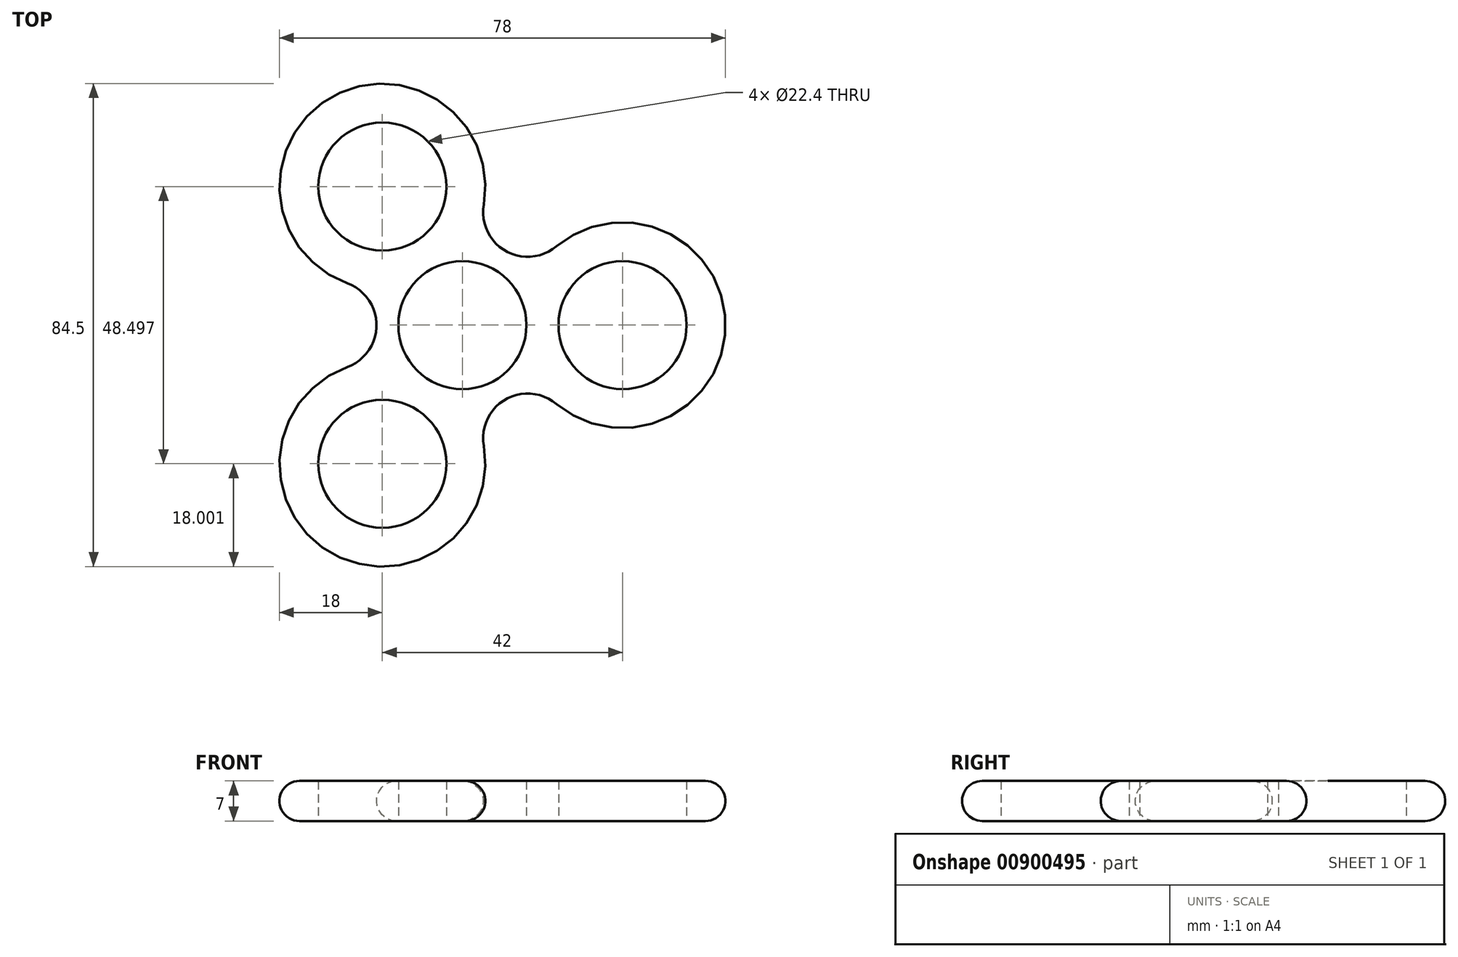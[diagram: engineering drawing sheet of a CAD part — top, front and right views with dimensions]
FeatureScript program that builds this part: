
annotation { "Feature Type Name" : "Feature", "Feature Type Description" : "" }
export const myFeature = defineFeature(function(context is Context, id is Id, definition is map)
    precondition{}
    {
        {
            assignVariable(context, id + "F0", {"name" : "w", "anyValue" : 7});
        }
        {
            var Q0;
            Q0=qCreatedBy(makeId("Top.planeOp"),FACE);
            var sketch = newSketch(context, id + "F1", { "sketchPlane" : qUnion([Q0])});
            skLineSegment(sketch, "E0", {"start": v(0, 0) * mm, "end": v(28, 0) * mm, "construction": true});
            skCircle(sketch, "E1", {"center": v(0, 0) * mm, "radius": 11.2 * mm});
            skCircle(sketch, "E2", {"center": v(28, 0) * mm, "radius": 11.2 * mm});
            skLineSegment(sketch, "E3", {"start": v(0, 0) * mm, "end": v(16.43, 13.79) * mm});
            skLineSegment(sketch, "E4", {"start": v(16.43, 13.79) * mm, "end": v(28, 0) * mm});
            skLineSegment(sketch, "E5", {"start": v(16.43, -13.79) * mm, "end": v(28, 0) * mm});
            skLineSegment(sketch, "E6", {"start": v(0, 0) * mm, "end": v(16.43, -13.79) * mm});
            skCircle(sketch, "E7", {"center": v(28, 0) * mm, "radius": 18 * mm});
            skCircle(sketch, "E8.cCircle", {"center": v(0, 0) * mm, "radius": 28 * mm, "construction": true});
            skLineSegment(sketch, "E8.0", {"start": v(28, 0) * mm, "end": v(14, -24.25) * mm, "construction": true});
            skLineSegment(sketch, "E8.1", {"start": v(14, -24.25) * mm, "end": v(-14, -24.25) * mm, "construction": true});
            skLineSegment(sketch, "E8.2", {"start": v(-14, -24.25) * mm, "end": v(-28, 0) * mm, "construction": true});
            skLineSegment(sketch, "E8.3", {"start": v(-28, 0) * mm, "end": v(-14, 24.25) * mm, "construction": true});
            skLineSegment(sketch, "E8.4", {"start": v(-14, 24.25) * mm, "end": v(14, 24.25) * mm, "construction": true});
            skLineSegment(sketch, "E8.5", {"start": v(14, 24.25) * mm, "end": v(28, 0) * mm, "construction": true});
            skCircle(sketch, "E9", {"center": v(-14, 24.25) * mm, "radius": 11.2 * mm});
            skCircle(sketch, "E10", {"center": v(-14, -24.25) * mm, "radius": 11.2 * mm});
            skLineSegment(sketch, "E11", {"start": v(0, 0) * mm, "end": v(-20.15, 7.33) * mm});
            skLineSegment(sketch, "E12", {"start": v(-20.15, 7.33) * mm, "end": v(-14, 24.25) * mm});
            skLineSegment(sketch, "E13", {"start": v(-14, 24.25) * mm, "end": v(3.73, 21.12) * mm});
            skLineSegment(sketch, "E14", {"start": v(3.73, 21.12) * mm, "end": v(0, 0) * mm});
            skLineSegment(sketch, "E15", {"start": v(0, 0) * mm, "end": v(-20.15, -7.33) * mm});
            skLineSegment(sketch, "E16", {"start": v(-20.15, -7.33) * mm, "end": v(-14, -24.25) * mm});
            skLineSegment(sketch, "E17", {"start": v(0, 0) * mm, "end": v(3.73, -21.12) * mm});
            skLineSegment(sketch, "E18", {"start": v(3.73, -21.12) * mm, "end": v(-14, -24.25) * mm});
            skCircle(sketch, "E19", {"center": v(-14, -24.25) * mm, "radius": 18 * mm});
            skCircle(sketch, "E20", {"center": v(-14, 24.25) * mm, "radius": 18 * mm});
            skLineSegment(sketch, "E21", {"start": v(3.73, 21.12) * mm, "end": v(8.02, 45.44) * mm, "construction": true});
            skArc(sketch, "E22", {"start": v(3.73, 21.12) * mm, "mid": v(7.5, 13) * mm, "end": v(16.43, 13.79) * mm});
            skLineSegment(sketch, "E23", {"start": v(-20.15, -7.33) * mm, "end": v(-52.36, -19.05) * mm, "construction": true});
            skArc(sketch, "E24", {"start": v(-20.15, -7.33) * mm, "mid": v(-15.02, 0) * mm, "end": v(-20.15, 7.33) * mm});
            skLineSegment(sketch, "E25", {"start": v(3.73, -21.12) * mm, "end": v(7.3, -41.37) * mm, "construction": true});
            skArc(sketch, "E26", {"start": v(3.73, -21.12) * mm, "mid": v(7.5, -13) * mm, "end": v(16.43, -13.79) * mm});
            skSolve(sketch);
        }
        {
            var Q0;
            {var subQ1=sQuery(id+"F1.wireOp",EDGE,"E4");var subQ4=sQuery(id+"F1.wireOp",EDGE,"E2");var subQ5=makeQuery(id+"F1.imprint","INTERSECT",VERTEX,{"derivedFrom":[subQ4,subQ1]});Q0=makeQuery(id+"F1.imprint","IMPRINT",FACE,{"disambiguationData":[TD([[makeQuery(id+"F1.imprint","IMPRINT",EDGE,{"disambiguationData":[TD([[subQ5,1.0]])],"derivedFrom":subQ4}),-1.0]])]});}
            var Q1;
            {var subQ5=sQuery(id+"F1.wireOp",EDGE,"E9");var subQ7=sQuery(id+"F1.wireOp",EDGE,"E12");var subQ9=makeQuery(id+"F1.imprint","INTERSECT",VERTEX,{"derivedFrom":[subQ5,subQ7]});Q1=makeQuery(id+"F1.imprint","IMPRINT",FACE,{"disambiguationData":[TD([[makeQuery(id+"F1.imprint","IMPRINT",EDGE,{"disambiguationData":[TD([[subQ9,1.0]])],"derivedFrom":subQ5}),-1.0]])]});}
            var Q2;
            {var subQ4=sQuery(id+"F1.wireOp",EDGE,"E16");var subQ6=sQuery(id+"F1.wireOp",EDGE,"E10");var subQ7=makeQuery(id+"F1.imprint","INTERSECT",VERTEX,{"derivedFrom":[subQ6,subQ4]});Q2=makeQuery(id+"F1.imprint","IMPRINT",FACE,{"disambiguationData":[TD([[makeQuery(id+"F1.imprint","IMPRINT",EDGE,{"disambiguationData":[TD([[subQ7,-1.0]])],"derivedFrom":subQ6}),-1.0]])]});}
            var Q3;
            {var subQ3=sQuery(id+"F1.wireOp",EDGE,"E1");var subQ6=sQuery(id+"F1.wireOp",EDGE,"E3");var subQ8=makeQuery(id+"F1.imprint","INTERSECT",VERTEX,{"derivedFrom":[subQ3,subQ6]});Q3=makeQuery(id+"F1.imprint","IMPRINT",FACE,{"disambiguationData":[TD([[makeQuery(id+"F1.imprint","IMPRINT",EDGE,{"disambiguationData":[TD([[subQ8,-1.0]])],"derivedFrom":subQ3}),-1.0]])]});}
            var Q4;
            {var subQ5=sQuery(id+"F1.wireOp",EDGE,"E1");var subQ7=sQuery(id+"F1.wireOp",EDGE,"E11");var subQ8=makeQuery(id+"F1.imprint","INTERSECT",VERTEX,{"derivedFrom":[subQ5,subQ7]});Q4=makeQuery(id+"F1.imprint","IMPRINT",FACE,{"disambiguationData":[TD([[makeQuery(id+"F1.imprint","IMPRINT",EDGE,{"disambiguationData":[TD([[subQ8,-1.0]])],"derivedFrom":subQ5}),-1.0]])]});}
            var Q5;
            {var subQ1=sQuery(id+"F1.wireOp",EDGE,"E17");var subQ3=sQuery(id+"F1.wireOp",EDGE,"E1");var subQ4=makeQuery(id+"F1.imprint","INTERSECT",VERTEX,{"derivedFrom":[subQ3,subQ1]});Q5=makeQuery(id+"F1.imprint","IMPRINT",FACE,{"disambiguationData":[TD([[makeQuery(id+"F1.imprint","IMPRINT",EDGE,{"disambiguationData":[TD([[subQ4,-1.0]])],"derivedFrom":subQ3}),-1.0]])]});}
            var Q6;
            {var subQ1=sQuery(id+"F1.wireOp",EDGE,"E12");var subQ6=sQuery(id+"F1.wireOp",EDGE,"E9");var subQ8=makeQuery(id+"F1.imprint","INTERSECT",VERTEX,{"derivedFrom":[subQ6,subQ1]});Q6=makeQuery(id+"F1.imprint","IMPRINT",FACE,{"disambiguationData":[TD([[makeQuery(id+"F1.imprint","IMPRINT",EDGE,{"disambiguationData":[TD([[subQ8,-1.0]])],"derivedFrom":subQ6}),-1.0]])]});}
            var Q7;
            {var subQ0=sQuery(id+"F1.wireOp",EDGE,"E20");var subQ1=sQuery(id+"F1.wireOp",EDGE,"E1");var subQ2=makeQuery(id+"F1.imprint","INTERSECT",VERTEX,{"derivedFrom":[subQ1,subQ0]});Q7=makeQuery(id+"F1.imprint","IMPRINT",FACE,{"disambiguationData":[TD([[makeQuery(id+"F1.imprint","IMPRINT",EDGE,{"disambiguationData":[TD([[subQ2,-1.0]])],"derivedFrom":subQ1}),-1.0]])]});}
            var Q8;
            {var subQ0=sQuery(id+"F1.wireOp",EDGE,"E14");var subQ1=sQuery(id+"F1.wireOp",EDGE,"E1");var subQ2=makeQuery(id+"F1.imprint","INTERSECT",VERTEX,{"derivedFrom":[subQ1,subQ0]});Q8=makeQuery(id+"F1.imprint","IMPRINT",FACE,{"disambiguationData":[TD([[makeQuery(id+"F1.imprint","IMPRINT",EDGE,{"disambiguationData":[TD([[subQ2,-1.0]])],"derivedFrom":subQ1}),-1.0]])]});}
            var Q9;
            {var subQ0=sQuery(id+"F1.wireOp",EDGE,"E15");var subQ1=sQuery(id+"F1.wireOp",EDGE,"E1");var subQ2=makeQuery(id+"F1.imprint","INTERSECT",VERTEX,{"derivedFrom":[subQ1,subQ0]});Q9=makeQuery(id+"F1.imprint","IMPRINT",FACE,{"disambiguationData":[TD([[makeQuery(id+"F1.imprint","IMPRINT",EDGE,{"disambiguationData":[TD([[subQ2,-1.0]])],"derivedFrom":subQ1}),-1.0]])]});}
            var Q10;
            {var subQ4=sQuery(id+"F1.wireOp",EDGE,"E10");var subQ6=sQuery(id+"F1.wireOp",EDGE,"E16");var subQ8=makeQuery(id+"F1.imprint","INTERSECT",VERTEX,{"derivedFrom":[subQ4,subQ6]});Q10=makeQuery(id+"F1.imprint","IMPRINT",FACE,{"disambiguationData":[TD([[makeQuery(id+"F1.imprint","IMPRINT",EDGE,{"disambiguationData":[TD([[subQ8,1.0]])],"derivedFrom":subQ4}),-1.0]])]});}
            var Q11;
            {var subQ0=sQuery(id+"F1.wireOp",EDGE,"E19");var subQ1=sQuery(id+"F1.wireOp",EDGE,"E1");var subQ2=makeQuery(id+"F1.imprint","INTERSECT",VERTEX,{"derivedFrom":[subQ1,subQ0]});Q11=makeQuery(id+"F1.imprint","IMPRINT",FACE,{"disambiguationData":[TD([[makeQuery(id+"F1.imprint","IMPRINT",EDGE,{"disambiguationData":[TD([[subQ2,-1.0]])],"derivedFrom":subQ1}),-1.0]])]});}
            var Q12;
            {var subQ0=sQuery(id+"F1.wireOp",EDGE,"E3");var subQ1=sQuery(id+"F1.wireOp",EDGE,"E1");var subQ2=makeQuery(id+"F1.imprint","INTERSECT",VERTEX,{"derivedFrom":[subQ1,subQ0]});Q12=makeQuery(id+"F1.imprint","IMPRINT",FACE,{"disambiguationData":[TD([[makeQuery(id+"F1.imprint","IMPRINT",EDGE,{"disambiguationData":[TD([[subQ2,1.0]])],"derivedFrom":subQ1}),-1.0]])]});}
            var Q13;
            {var subQ1=sQuery(id+"F1.wireOp",EDGE,"E4");var subQ4=sQuery(id+"F1.wireOp",EDGE,"E2");var subQ5=makeQuery(id+"F1.imprint","INTERSECT",VERTEX,{"derivedFrom":[subQ4,subQ1]});Q13=makeQuery(id+"F1.imprint","IMPRINT",FACE,{"disambiguationData":[TD([[makeQuery(id+"F1.imprint","IMPRINT",EDGE,{"disambiguationData":[TD([[subQ5,-1.0]])],"derivedFrom":subQ4}),-1.0]])]});}
            var Q14;
            {var subQ0=sQuery(id+"F1.wireOp",EDGE,"E7");var subQ1=sQuery(id+"F1.wireOp",EDGE,"E1");var subQ2=makeQuery(id+"F1.imprint","INTERSECT",VERTEX,{"derivedFrom":[subQ1,subQ0]});Q14=makeQuery(id+"F1.imprint","IMPRINT",FACE,{"disambiguationData":[TD([[makeQuery(id+"F1.imprint","IMPRINT",EDGE,{"disambiguationData":[TD([[subQ2,1.0]])],"derivedFrom":subQ1}),-1.0]])]});}
            extrude(context, id + "F2", {"entities" : qUnion([Q0, Q1, Q2, Q3, Q4, Q5, Q6, Q7, Q8, Q9, Q10, Q11, Q12, Q13, Q14]), "endBound" : BoundingType.SYMMETRIC, "depth" : (getVariable(context, 'w')) * mm, "offsetDistance" : 25 * mm});
        }
        {
            var Q0;
            Q0=makeQuery(id+"F2.opExtrude","CAP_EDGE",EDGE,{"disambiguationData":[OSD([sQuery(id+"F1.wireOp",EDGE,"E19")])],"isStart":false});
            var Q1;
            Q1=makeQuery(id+"F2.opExtrude","CAP_EDGE",EDGE,{"disambiguationData":[OSD([sQuery(id+"F1.wireOp",EDGE,"E20")])],"isStart":false});
            var Q2;
            Q2=makeQuery(id+"F2.opExtrude","CAP_EDGE",EDGE,{"disambiguationData":[OSD([sQuery(id+"F1.wireOp",EDGE,"E7")])],"isStart":false});
            var Q3;
            Q3=makeQuery(id+"F2.opExtrude","CAP_EDGE",EDGE,{"disambiguationData":[OSD([sQuery(id+"F1.wireOp",EDGE,"E19")])],"isStart":true});
            var Q4;
            Q4=makeQuery(id+"F2.opExtrude","CAP_EDGE",EDGE,{"disambiguationData":[OSD([sQuery(id+"F1.wireOp",EDGE,"E7")])],"isStart":true});
            var Q5;
            Q5=makeQuery(id+"F2.opExtrude","CAP_EDGE",EDGE,{"disambiguationData":[OSD([sQuery(id+"F1.wireOp",EDGE,"E20")])],"isStart":true});
            var Q6;
            Q6=makeQuery(id+"F2.opExtrude","CAP_EDGE",EDGE,{"disambiguationData":[OSD([sQuery(id+"F1.wireOp",EDGE,"DmTfLF0m-c8a2-DMid-hrdA-jiZlNyXnCwRp")])],"isStart":false});
            var Q7;
            Q7=makeQuery(id+"F2.opExtrude","CAP_EDGE",EDGE,{"disambiguationData":[OSD([sQuery(id+"F1.wireOp",EDGE,"EfMKk5JN-c9Zu-Lmpf-7oAc-OTBsgBrKdwgi")])],"isStart":false});
            var Q8;
            Q8=makeQuery(id+"F2.opExtrude","CAP_EDGE",EDGE,{"disambiguationData":[OSD([sQuery(id+"F1.wireOp",EDGE,"kHU36Bgz-RPuo-XmWi-LJc6-9ikQLt18EW8G")])],"isStart":false});
            var Q9;
            Q9=makeQuery(id+"F2.opExtrude","CAP_EDGE",EDGE,{"disambiguationData":[OSD([sQuery(id+"F1.wireOp",EDGE,"DmTfLF0m-c8a2-DMid-hrdA-jiZlNyXnCwRp")])],"isStart":true});
            var Q10;
            Q10=makeQuery(id+"F2.opExtrude","CAP_EDGE",EDGE,{"disambiguationData":[OSD([sQuery(id+"F1.wireOp",EDGE,"EfMKk5JN-c9Zu-Lmpf-7oAc-OTBsgBrKdwgi")])],"isStart":true});
            var Q11;
            Q11=makeQuery(id+"F2.opExtrude","CAP_EDGE",EDGE,{"disambiguationData":[OSD([sQuery(id+"F1.wireOp",EDGE,"kHU36Bgz-RPuo-XmWi-LJc6-9ikQLt18EW8G")])],"isStart":true});
            fillet(context, id + "F3", {"entities" : qUnion([Q0, Q1, Q2, Q3, Q4, Q5, Q6, Q7, Q8, Q9, Q10, Q11]), "radius" : (getVariable(context, 'w') / 2) * mm, "tangentPropagation" : true, "allowEdgeOverflow" : false});
        }
    });
